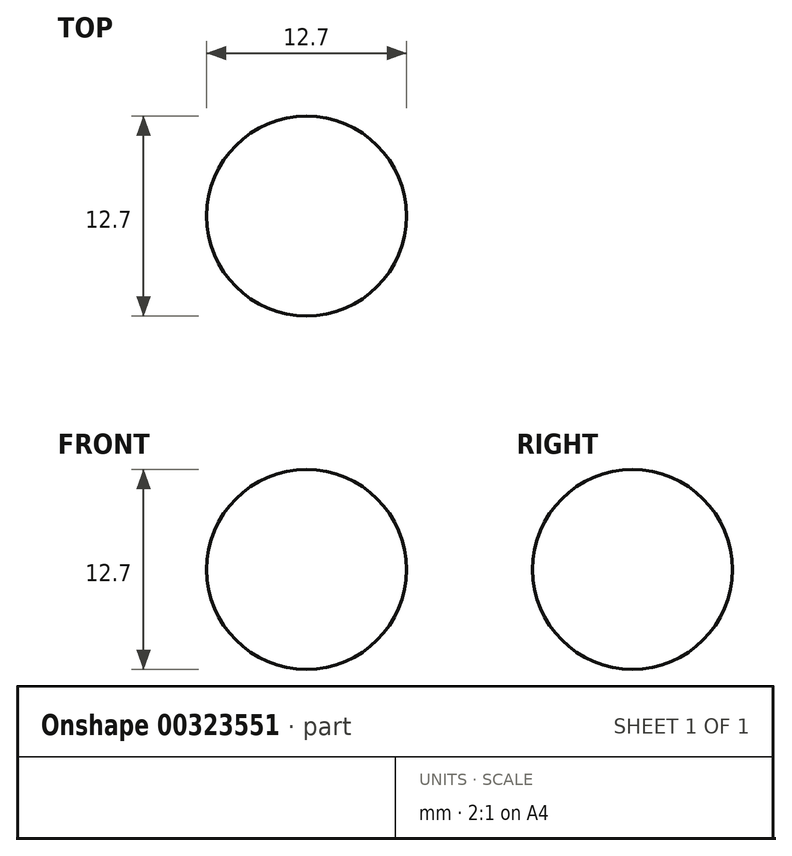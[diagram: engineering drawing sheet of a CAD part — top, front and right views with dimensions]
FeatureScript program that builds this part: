
annotation { "Feature Type Name" : "Feature", "Feature Type Description" : "" }
export const myFeature = defineFeature(function(context is Context, id is Id, definition is map)
    precondition{}
    {
        {
            var Q0;
            Q0=qCreatedBy(makeId("Top.planeOp"),FACE);
            var sketch = newSketch(context, id + "F0", { "sketchPlane" : qUnion([Q0])});
            skCircle(sketch, "E0", {"center": v(0, 0) * mm, "radius": 6.35 * mm});
            skLineSegment(sketch, "E1", {"start": v(0, 6.35) * mm, "end": v(0, -6.35) * mm});
            skSolve(sketch);
        }
        {
            var Q0;
            {var subQ0=sQuery(id+"F0.wireOp",EDGE,"E1");Q0=makeQuery(id+"F0.imprint","IMPRINT",FACE,{"disambiguationData":[TD([[makeQuery(id+"F0.imprint","IMPRINT",EDGE,{"derivedFrom":subQ0}),1.0]])]});}
            var Q1;
            Q1=sQuery(id+"F0.wireOp",EDGE,"E1");
            revolve(context, id + "F1", {"entities" : qUnion([Q0]), "axis" : qUnion([Q1]), "revolveType" : RevolveType.FULL});
        }
    });
